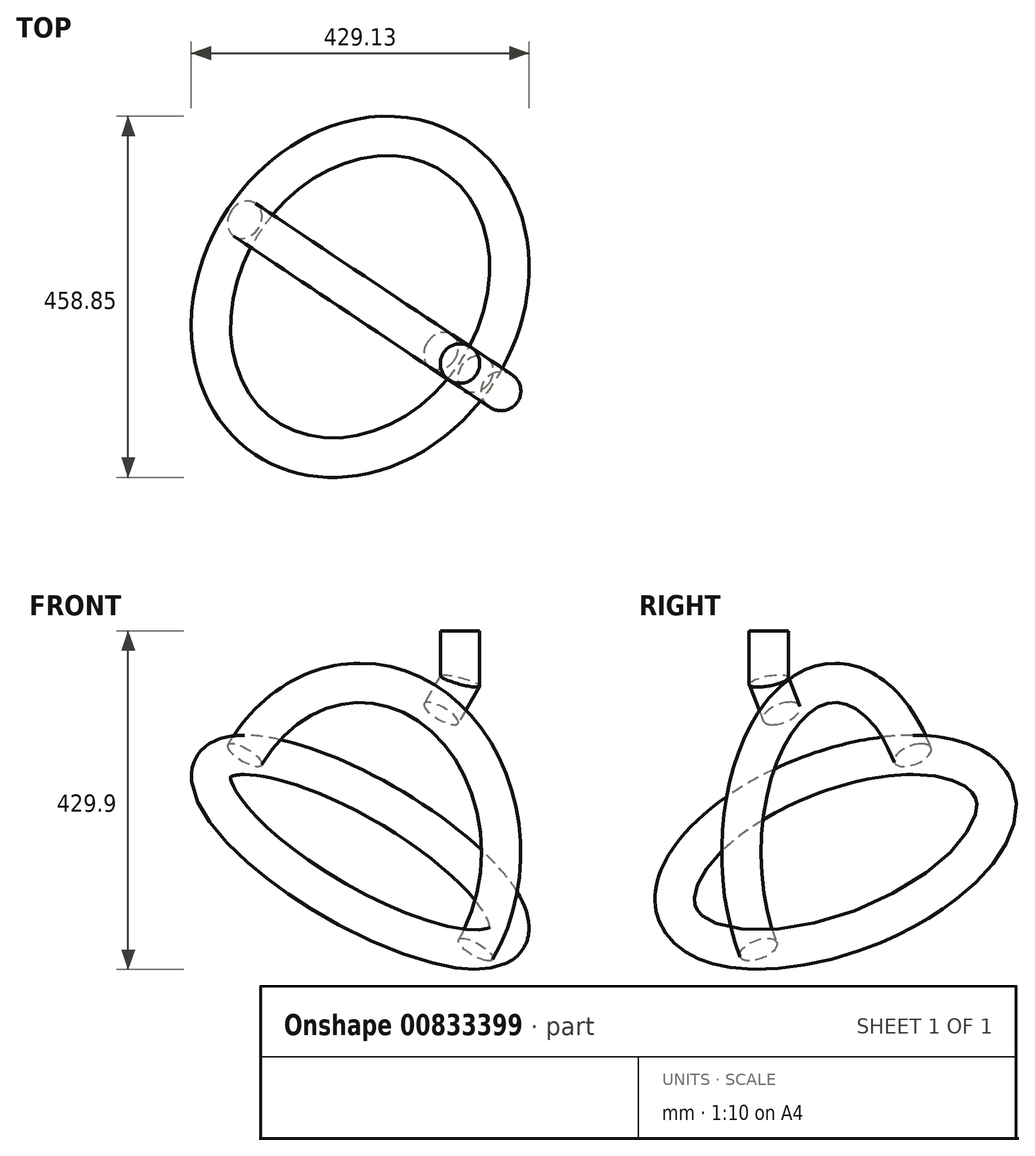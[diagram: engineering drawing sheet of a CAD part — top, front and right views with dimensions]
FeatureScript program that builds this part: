
annotation { "Feature Type Name" : "Feature", "Feature Type Description" : "" }
export const myFeature = defineFeature(function(context is Context, id is Id, definition is map)
    precondition{}
    {
        {
            var Q0;
            Q0=qCreatedBy(makeId("Front.planeOp"),FACE);
            var sketch = newSketch(context, id + "F0", { "sketchPlane" : qUnion([Q0])});
            skLineSegment(sketch, "E0", {"start": v(0, 0) * mm, "end": v(0, -63.5) * mm});
            skLineSegment(sketch, "E1", {"start": v(152.5, -281.3) * mm, "end": v(329.03, -157.7) * mm});
            skLineSegment(sketch, "E2", {"start": v(152.5, -281.3) * mm, "end": v(-24.02, -404.9) * mm});
            skArc(sketch, "E3", {"start": v(329.03, -157.7) * mm, "mid": v(28.97, -104.87) * mm, "end": v(-24.02, -404.9) * mm});
            skLineSegment(sketch, "E4", {"start": v(0, -63.5) * mm, "end": v(28.97, -104.87) * mm});
            skLineSegment(sketch, "E5", {"start": v(28.97, -104.87) * mm, "end": v(152.57, -281.4) * mm});
            skCircle(sketch, "E6", {"center": v(-24.02, -404.9) * mm, "radius": 25 * mm});
            skSolve(sketch);
        }
        {
            var Q0;
            Q0=sQuery(id+"F0.wireOp",VERTEX,"97wq7kTM-Wat1-zyJu-AWVl-G3QsEm7D3rIj.end");
            var Q1;
            Q1=sQuery(id+"F0.wireOp",EDGE,"97wq7kTM-Wat1-zyJu-AWVl-G3QsEm7D3rIj");
            var Q2;
            Q2=sQuery(id+"F0.wireOp",VERTEX,"E1.start");
            var Q3;
            Q3=sQuery(id+"F0.wireOp",EDGE,"E5");
            cPlane(context, id + "F1", {"entities" : qUnion([Q0, Q1, Q2, Q3]), "cplaneType" : CPlaneType.LINE_POINT, "offset" : 25.4 * mm, "width" : 152.4 * mm, "height" : 152.4 * mm});
        }
        {
            var Q0;
            Q0=qCreatedBy(id+"F1.planeOp",FACE);
            var sketch = newSketch(context, id + "F2", { "sketchPlane" : qUnion([Q0])});
            skCircle(sketch, "E7", {"center": v(-36.25, 0.07) * mm, "radius": 215.5 * mm});
            skCircle(sketch, "E8", {"center": v(-251.74, 0) * mm, "radius": 25 * mm});
            skSolve(sketch);
        }
        {
            var Q0;
            Q0=qCreatedBy(makeId("Top.planeOp"),FACE);
            var sketch = newSketch(context, id + "F3", { "sketchPlane" : qUnion([Q0])});
            skCircle(sketch, "E9", {"center": v(0, 0) * mm, "radius": 25 * mm});
            skSolve(sketch);
        }
        {
            var Q0;
            Q0=makeQuery(id+"F3.imprint","IMPRINT",FACE,{"disambiguationData":[TD([[makeQuery(id+"F3.imprint","IMPRINT",EDGE,{"derivedFrom":sQuery(id+"F3.wireOp",EDGE,"E9")}),1.0]])]});
            var Q1;
            Q1=sQuery(id+"F3.wireOp",EDGE,"E9");
            var Q2;
            Q2=sQuery(id+"F0.wireOp",EDGE,"E0");
            var Q3;
            Q3=sQuery(id+"F0.wireOp",EDGE,"E4");
            sweep(context, id + "F4", {"profiles" : qUnion([Q0]), "surfaceProfiles" : qUnion([Q1]), "path" : qUnion([Q2, Q3])});
        }
        {
            var Q0;
            {var subQ0=sQuery(id+"F2.wireOp",EDGE,"E8");var subQ1=sQuery(id+"F2.wireOp",EDGE,"E7");var subQ2=makeQuery(id+"F2.imprint","INTERSECT",VERTEX,{"disambiguationData":[OD(0.0)],"derivedFrom":[subQ1,subQ0]});Q0=makeQuery(id+"F2.imprint","IMPRINT",FACE,{"disambiguationData":[TD([[makeQuery(id+"F2.imprint","IMPRINT",EDGE,{"disambiguationData":[TD([[subQ2,-1.0]])],"derivedFrom":subQ1}),-1.0]])]});}
            var Q1;
            {var subQ0=sQuery(id+"F2.wireOp",EDGE,"E8");var subQ1=sQuery(id+"F2.wireOp",EDGE,"E7");var subQ2=makeQuery(id+"F2.imprint","INTERSECT",VERTEX,{"disambiguationData":[OD(0.0)],"derivedFrom":[subQ1,subQ0]});Q1=makeQuery(id+"F2.imprint","IMPRINT",FACE,{"disambiguationData":[TD([[makeQuery(id+"F2.imprint","IMPRINT",EDGE,{"disambiguationData":[TD([[subQ2,-1.0]])],"derivedFrom":subQ1}),1.0]])]});}
            var Q2;
            Q2=sQuery(id+"F0.wireOp",EDGE,"E3");
            sweep(context, id + "F5", {"profiles" : qUnion([Q0, Q1]), "path" : qUnion([Q2])});
        }
        {
            var Q0;
            {var subQ0=sQuery(id+"F0.wireOp",EDGE,"E3");var subQ1=sQuery(id+"F0.wireOp",EDGE,"E2");var subQ2=makeQuery(id+"F0.imprint","INTERSECT",VERTEX,{"derivedFrom":[subQ1,subQ0]});Q0=makeQuery(id+"F0.imprint","IMPRINT",FACE,{"disambiguationData":[TD([[makeQuery(id+"F0.imprint","IMPRINT",EDGE,{"disambiguationData":[TD([[subQ2,1.0]])],"derivedFrom":subQ1}),1.0]])]});}
            var Q1;
            {var subQ0=sQuery(id+"F0.wireOp",EDGE,"E3");var subQ1=sQuery(id+"F0.wireOp",EDGE,"E2");var subQ2=makeQuery(id+"F0.imprint","INTERSECT",VERTEX,{"derivedFrom":[subQ1,subQ0]});Q1=makeQuery(id+"F0.imprint","IMPRINT",FACE,{"disambiguationData":[TD([[makeQuery(id+"F0.imprint","IMPRINT",EDGE,{"disambiguationData":[TD([[subQ2,1.0]])],"derivedFrom":subQ1}),-1.0]])]});}
            var Q2;
            Q2=sQuery(id+"F2.wireOp",EDGE,"E7");
            sweep(context, id + "F6", {"profiles" : qUnion([Q0, Q1]), "path" : qUnion([Q2])});
        }
        {
            var Q0;
            Q0=makeQuery(id+"F5.opSweep","SWEPT_BODY",BODY,{"disambiguationData":[OSD([sQuery(id+"F0.wireOp",EDGE,"E3"),sQuery(id+"F2.wireOp",EDGE,"E8")])]});
            var Q1;
            Q1=makeQuery(id+"F6.opSweep","SWEPT_BODY",BODY,{"disambiguationData":[OSD([sQuery(id+"F0.wireOp",EDGE,"E6"),sQuery(id+"F2.wireOp",EDGE,"E7")])]});
            var Q2;
            Q2=makeQuery(id+"F4.opSweep","SWEPT_BODY",BODY,{"disambiguationData":[OSD([sQuery(id+"F0.wireOp",EDGE,"E4"),sQuery(id+"F3.wireOp",EDGE,"E9")])]});
            var Q3;
            Q3=sQuery(id+"F0.wireOp",EDGE,"E0");
            transform(context, id + "F7", {"entities" : qUnion([Q0, Q1, Q2]), "transformType" : TransformType.ROTATION, "transformAxis" : qUnion([Q3]), "angle" : 213.75 * degree, "makeCopy" : false});
        }
    });
